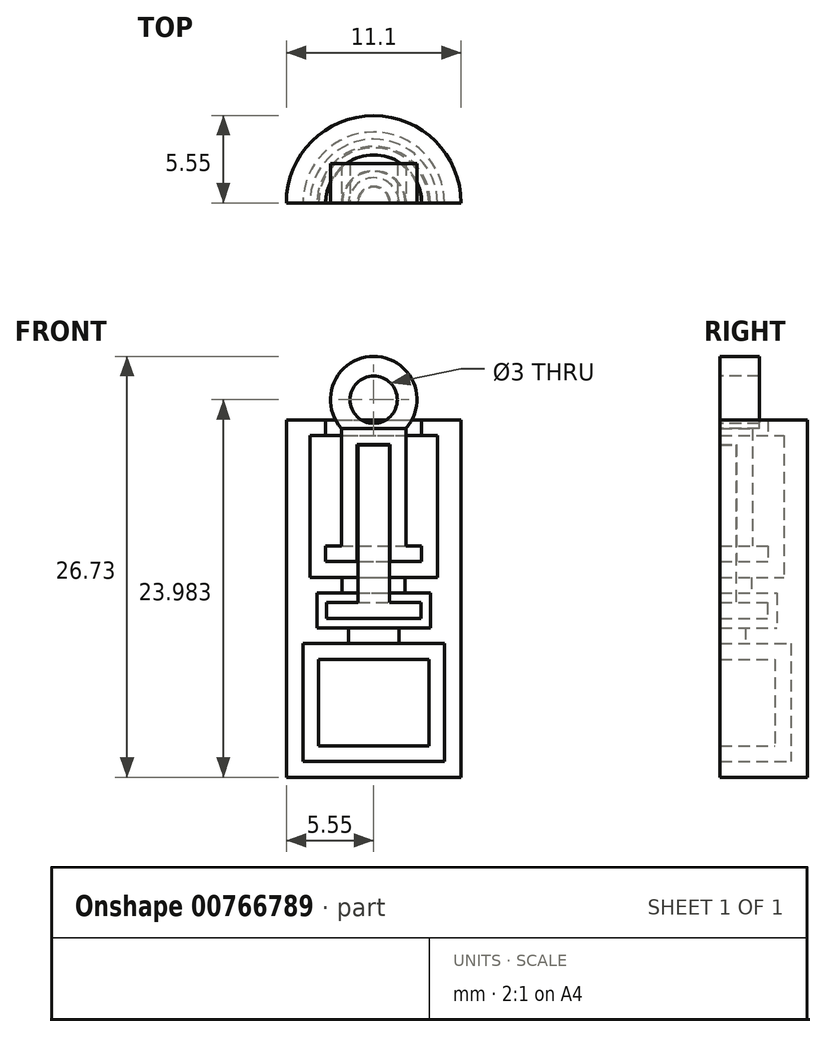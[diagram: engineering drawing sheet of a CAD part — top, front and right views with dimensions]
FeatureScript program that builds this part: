
annotation { "Feature Type Name" : "Feature", "Feature Type Description" : "" }
export const myFeature = defineFeature(function(context is Context, id is Id, definition is map)
    precondition{}
    {
        {
            var Q0;
            Q0=qCreatedBy(makeId("Front.planeOp"),FACE);
            var sketch = newSketch(context, id + "F0", { "sketchPlane" : qUnion([Q0])});
            skLineSegment(sketch, "E0.bottom", {"start": v(3, 0.5) * mm, "end": v(-3, 0.5) * mm});
            skLineSegment(sketch, "E0.top", {"start": v(3, -0.5) * mm, "end": v(-3, -0.5) * mm});
            skLineSegment(sketch, "E0.left", {"start": v(3, 0.5) * mm, "end": v(3, -0.5) * mm});
            skLineSegment(sketch, "E0.right", {"start": v(-3, 0.5) * mm, "end": v(-3, -0.5) * mm});
            skPoint(sketch, "E0.middle", {"position": v(0, 0) * mm});
            skLineSegment(sketch, "E1.bottom", {"start": v(-1, 0.5) * mm, "end": v(1, 0.5) * mm});
            skLineSegment(sketch, "E1.top", {"start": v(-1, 10.5) * mm, "end": v(1, 10.5) * mm});
            skLineSegment(sketch, "E1.left", {"start": v(-1, 0.5) * mm, "end": v(-1, 10.5) * mm});
            skLineSegment(sketch, "E1.right", {"start": v(1, 0.5) * mm, "end": v(1, 10.5) * mm});
            skLineSegment(sketch, "E2", {"start": v(-1.05, 3.1) * mm, "end": v(-3.05, 3.1) * mm});
            skLineSegment(sketch, "E3", {"start": v(-3.05, 3.1) * mm, "end": v(-3.05, 4.1) * mm});
            skLineSegment(sketch, "E4", {"start": v(-3.05, 4.1) * mm, "end": v(-2.05, 4.1) * mm});
            skLineSegment(sketch, "E5", {"start": v(-2.05, 4.1) * mm, "end": v(-2.05, 11.55) * mm});
            skLineSegment(sketch, "E6", {"start": v(-1.05, 3.1) * mm, "end": v(-1.05, 10.55) * mm});
            skLineSegment(sketch, "E7", {"start": v(1.05, 10.55) * mm, "end": v(1.05, 3.1) * mm});
            skLineSegment(sketch, "E8", {"start": v(1.05, 3.1) * mm, "end": v(3.05, 3.1) * mm});
            skLineSegment(sketch, "E9", {"start": v(3.05, 3.1) * mm, "end": v(3.05, 4.1) * mm});
            skLineSegment(sketch, "E10", {"start": v(3.05, 4.1) * mm, "end": v(2.05, 4.1) * mm});
            skLineSegment(sketch, "E11", {"start": v(2.05, 4.1) * mm, "end": v(2.05, 11.55) * mm});
            skLineSegment(sketch, "E12", {"start": v(-2, 2.1) * mm, "end": v(-12.95, 2.1) * mm});
            skLineSegment(sketch, "E13", {"start": v(-12.95, 2.1) * mm, "end": v(-12.95, 11.1) * mm});
            skLineSegment(sketch, "E14", {"start": v(-12.95, 11.1) * mm, "end": v(-11.95, 11.1) * mm});
            skLineSegment(sketch, "E15", {"start": v(-11.95, 11.1) * mm, "end": v(-11.95, 12.1) * mm});
            skLineSegment(sketch, "E16", {"start": v(-11.95, 12.1) * mm, "end": v(-14.45, 12.1) * mm});
            skLineSegment(sketch, "E17", {"start": v(-14.45, 12.1) * mm, "end": v(-14.45, -10.6) * mm});
            skLineSegment(sketch, "E18", {"start": v(-3.6, -1.1) * mm, "end": v(-3.6, 1.1) * mm});
            skLineSegment(sketch, "E19", {"start": v(-3.6, 1.1) * mm, "end": v(-2, 1.1) * mm});
            skLineSegment(sketch, "E20", {"start": v(-2, 1.1) * mm, "end": v(-2, 2.1) * mm});
            skLineSegment(sketch, "E21", {"start": v(3.6, -1.1) * mm, "end": v(3.6, 1.1) * mm});
            skLineSegment(sketch, "E22", {"start": v(3.6, 1.1) * mm, "end": v(2, 1.1) * mm});
            skLineSegment(sketch, "E23", {"start": v(2, 1.1) * mm, "end": v(2, 2.1) * mm});
            skLineSegment(sketch, "E24", {"start": v(2, 2.1) * mm, "end": v(4.05, 2.1) * mm});
            skLineSegment(sketch, "E25", {"start": v(4.05, 2.1) * mm, "end": v(4.05, 11.1) * mm});
            skLineSegment(sketch, "E26", {"start": v(4.05, 11.1) * mm, "end": v(3.05, 11.1) * mm});
            skLineSegment(sketch, "E27", {"start": v(3.05, 11.1) * mm, "end": v(3.05, 12.1) * mm});
            skLineSegment(sketch, "E28", {"start": v(3.05, 12.1) * mm, "end": v(5.55, 12.1) * mm});
            skLineSegment(sketch, "E29", {"start": v(5.55, 12.1) * mm, "end": v(5.55, -10.6) * mm});
            skLineSegment(sketch, "E30", {"start": v(-1.05, 10.55) * mm, "end": v(1.05, 10.55) * mm});
            skCircle(sketch, "E31", {"center": v(0, 13.38) * mm, "radius": 1.5 * mm});
            skCircle(sketch, "E32", {"center": v(0, 13.38) * mm, "radius": 2.75 * mm});
            skLineSegment(sketch, "E33", {"start": v(-2.05, 11.55) * mm, "end": v(2.05, 11.55) * mm});
            skLineSegment(sketch, "E34", {"start": v(-3.6, -1.1) * mm, "end": v(-1.6, -1.1) * mm});
            skLineSegment(sketch, "E35", {"start": v(-1.6, -1.1) * mm, "end": v(-1.6, -2.1) * mm});
            skLineSegment(sketch, "E36", {"start": v(-1.6, -2.1) * mm, "end": v(-3.6, -2.1) * mm});
            skLineSegment(sketch, "E37", {"start": v(-3.6, -2.1) * mm, "end": v(-3.6, -9.6) * mm});
            skLineSegment(sketch, "E38", {"start": v(-3.6, -9.6) * mm, "end": v(4.5, -9.6) * mm});
            skLineSegment(sketch, "E39", {"start": v(4.5, -9.6) * mm, "end": v(4.5, -2.1) * mm});
            skLineSegment(sketch, "E40", {"start": v(4.5, -2.1) * mm, "end": v(1.6, -2.1) * mm});
            skLineSegment(sketch, "E41", {"start": v(1.6, -2.1) * mm, "end": v(1.6, -1.1) * mm});
            skLineSegment(sketch, "E42", {"start": v(1.6, -1.1) * mm, "end": v(3.6, -1.1) * mm});
            skLineSegment(sketch, "E43", {"start": v(-14.45, -10.6) * mm, "end": v(5.55, -10.6) * mm});
            skLineSegment(sketch, "E44", {"start": v(-0.6, -0.5) * mm, "end": v(-0.6, -3.1) * mm});
            skLineSegment(sketch, "E45", {"start": v(-0.6, -3.1) * mm, "end": v(-2.6, -3.1) * mm});
            skLineSegment(sketch, "E46", {"start": v(-2.6, -3.1) * mm, "end": v(-2.6, -8.6) * mm});
            skLineSegment(sketch, "E47", {"start": v(-2.6, -8.6) * mm, "end": v(3.5, -8.6) * mm});
            skLineSegment(sketch, "E48", {"start": v(3.5, -8.6) * mm, "end": v(3.5, -3.1) * mm});
            skLineSegment(sketch, "E49", {"start": v(3.5, -3.1) * mm, "end": v(0.6, -3.1) * mm});
            skLineSegment(sketch, "E50", {"start": v(0.6, -3.1) * mm, "end": v(0.6, -0.5) * mm});
            skLineSegment(sketch, "E51", {"start": v(0, -10.6) * mm, "end": v(0, 11.55) * mm});
            skLineSegment(sketch, "E52", {"start": v(-0.6, -3.1) * mm, "end": v(0.6, -3.1) * mm});
            skPoint(sketch, "E53", {"position": v(0, -3.1) * mm});
            skSolve(sketch);
        }
        {
            var Q0;
            {var subQ0=sQuery(id+"F0.wireOp",EDGE,"E48");Q0=makeQuery(id+"F0.imprint","IMPRINT",FACE,{"disambiguationData":[TD([[makeQuery(id+"F0.imprint","IMPRINT",EDGE,{"derivedFrom":subQ0}),1.0]])]});}
            var Q1;
            {var subQ0=sQuery(id+"F0.wireOp",EDGE,"E0.left");Q1=makeQuery(id+"F0.imprint","IMPRINT",FACE,{"disambiguationData":[TD([[makeQuery(id+"F0.imprint","IMPRINT",EDGE,{"derivedFrom":subQ0}),-1.0]])]});}
            var Q2;
            {var subQ0=sQuery(id+"F0.wireOp",EDGE,"E1.right");Q2=makeQuery(id+"F0.imprint","IMPRINT",FACE,{"disambiguationData":[TD([[makeQuery(id+"F0.imprint","IMPRINT",EDGE,{"derivedFrom":subQ0}),1.0]])]});}
            var Q3;
            {var subQ1=sQuery(id+"F0.wireOp",EDGE,"E7");Q3=makeQuery(id+"F0.imprint","IMPRINT",FACE,{"disambiguationData":[TD([[makeQuery(id+"F0.imprint","IMPRINT",EDGE,{"derivedFrom":subQ1}),1.0]])]});}
            var Q4;
            Q4=makeQuery(id+"F0.imprint","IMPRINT",FACE,{"disambiguationData":[TD([[makeQuery(id+"F0.imprint","IMPRINT",EDGE,{"derivedFrom":sQuery(id+"F0.wireOp",EDGE,"E21")}),-1.0]])]});
            var Q5;
            {var subQ0=sQuery(id+"F0.wireOp",EDGE,"E33");var subQ3=sQuery(id+"F0.wireOp",EDGE,"E51");var subQ5=makeQuery(id+"F0.imprint","INTERSECT",VERTEX,{"derivedFrom":[subQ0,subQ3]});Q5=makeQuery(id+"F0.imprint","IMPRINT",FACE,{"disambiguationData":[TD([[makeQuery(id+"F0.imprint","IMPRINT",EDGE,{"disambiguationData":[TD([[subQ5,1.0]])],"derivedFrom":subQ3}),-1.0]])]});}
            var Q6;
            Q6=sQuery(id+"F0.wireOp",EDGE,"E51");
            revolve(context, id + "F1", {"surfaceOperationType" : NewSurfaceOperationType.NEW, "entities" : qUnion([Q0, Q1, Q2, Q3, Q4, Q5]), "axis" : qUnion([Q6]), "revolveType" : RevolveType.ONE_DIRECTION, "angle" : 180 * degree});
        }
        {
            var Q0;
            Q0=makeQuery(id+"F0.imprint","IMPRINT",FACE,{"disambiguationData":[TD([[makeQuery(id+"F0.imprint","IMPRINT",EDGE,{"derivedFrom":sQuery(id+"F0.wireOp",EDGE,"E31")}),-1.0]])]});
            extrude(context, id + "F2", {"entities" : qUnion([Q0]), "oppositeDirection" : true, "depth" : 2.5 * mm, "offsetDistance" : 25 * mm});
        }
    });
